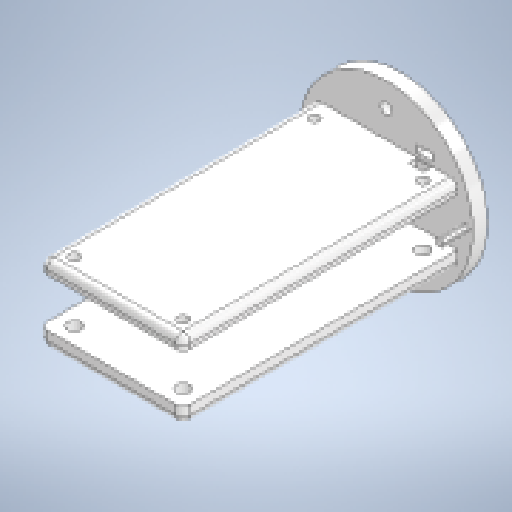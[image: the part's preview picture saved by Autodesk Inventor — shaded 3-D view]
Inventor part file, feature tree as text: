
AUTODESK INVENTOR PART (.ipt)
format: ipt  version: 2023 (Build 270158000, 158)  size: 263,680 bytes
history: native  units: in
note: dims shown in document units (in); Inventor stores cm internally (conversion verified against a paired STEP export)
features: other x11, sketch x9, reference x8, extrude x6, fillet x3, hole x3
ambient origin geometry x8: Origin, YZ Plane, XZ Plane, XY Plane, X Axis, Y Axis, Z Axis, Center Point
bodies: Solid1 (feature_tree)
feature tree (40):
  extrude  "Extrusion1"  Depth=0.25in TaperAngle=0.0deg
  extrude  "Extrusion2"  Depth=2.45in
  fillet  "Fillet1"  Radius=1.225in
  fillet  "Fillet2"  Radius=0.4125in
  hole  "Hole1"  [1 undecoded]
  hole  "Hole2"  [1 undecoded]
  hole  "Hole3"  [1 undecoded]
  extrude  "Extrusion4"  Depth=0.125in
  extrude  "Extrusion5"  Depth=0.297in
  extrude  "Extrusion6"  Depth=0.297in
  extrude  "Extrusion7"  Depth=0.0394in
  fillet  "Fillet4"  Radius=0.297in
  sketch  "Sketch1"  dims[d0=2.975in d1=0.25in d2=0.0in]
  sketch  "Sketch2"  dims[d3=0.283in d4=2.45in d5=1.225in d6=0.4125in]
  sketch  "Sketch3"  dims[d7=4.7in d8=0.0in d9=0.125in]
  sketch  "Sketch4"  dims[d10=2.45in d11=1.225in]
  reference  "Reference1"
  reference  "Reference2"
  reference  "Reference3"
  reference  "Reference4"
  sketch  "Sketch5"  dims[d12=0.4125in d13=0.2in]
  reference  "Reference5"
  reference  "Reference6"
  sketch  "Sketch7"  dims[d14=0.125in d15=0.297in]
  reference  "Reference10"
  reference  "Reference11"
  sketch  "Sketch8"  dims[d16=0.297in d17=0.297in]
  sketch  "Sketch9"  dims[d18=0.297in d19=0.297in]
  sketch  "Sketch10"  dims[d20=0.297in d21=0.297in d22=0.297in d23=0.23in d24=0.75in d25=0.332in d26=0.25in d27=0.5635in d28=1.0in d29=0.8108in d30=0.177in d31=0.75in d32=0.332in d33=0.25in d34=0.5635in d35=1.0in d36=0.8108in d37=0.177in d38=0.75in d39=0.332in d40=0.25in d41=0.5635in d42=1.0in d43=0.8108in d51=0.1575in d53=0.0197in d54=1.5748in d55=0.7874in d56=0.1181in d57=0.0in d58=0.25in d59=0.125in d60=0.0in d61=0.07in d62=0.0in d63=0.0in d64=0.0in d66=0.0in d67=0.025in d68=0.125in d69=1.0in d70=0.0in d71=0.125in d72=0.125in d73=1.4325in d74=1.4875in d75=0.005in d76=0.25in d77=0.0in d78=0.0394in d79=0.0625in]
  other  "<userpath>\Documents\ETS\RockETS\Certification JEEP\Avionics\StackAvionics_V2.iam"
  other  "StackAvionics_V2.iam"
  other  "94639A404_Off-White Nylon Unthreaded Spacer:2"
  other  "94639A404_Off-White Nylon Unthreaded Spacer:3"
  other  "94639A404_Off-White Nylon Unthreaded Spacer:4"
  other  "94639A404_Off-White Nylon Unthreaded Spacer:1"
  other  "<userpath>\Documents\ETS\RockETS\Certification JEEP\Avionics\FrontEnd_IRIS.iam"
  other  "FrontEnd_IRIS.iam"
  other  "CoupleurAvionics:1"
  other  "92395A324_Brass Screw-to-Expand Inserts:2"
  other  "BatteryHolder_DigiKEY:1"
note: 3 required parameter values undecoded (feature->parameter linkage not recoverable at this tier; creation-order binding heuristic only, values carry confidence <= 0.55)
